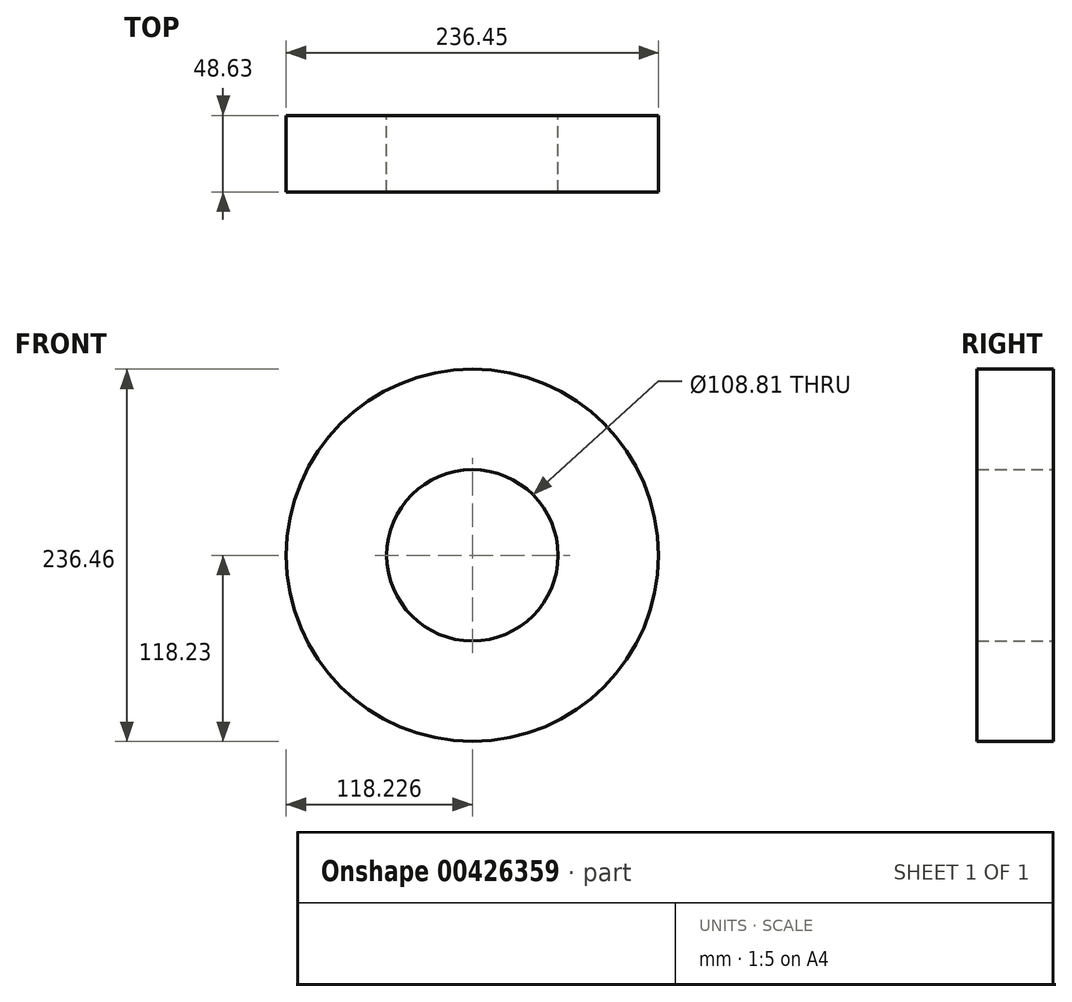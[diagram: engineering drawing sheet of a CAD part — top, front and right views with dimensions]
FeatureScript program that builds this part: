
annotation { "Feature Type Name" : "Feature", "Feature Type Description" : "" }
export const myFeature = defineFeature(function(context is Context, id is Id, definition is map)
    precondition{}
    {
        {
            var Q0;
            Q0=qCreatedBy(makeId("Top.planeOp"),FACE);
            var sketch = newSketch(context, id + "F0", { "sketchPlane" : qUnion([Q0])});
            skLineSegment(sketch, "E0.bottom", {"start": v(0, 0) * mm, "end": v(63.82, 0) * mm});
            skLineSegment(sketch, "E0.top", {"start": v(0, 48.63) * mm, "end": v(63.82, 48.63) * mm});
            skLineSegment(sketch, "E0.left", {"start": v(0, 0) * mm, "end": v(0, 48.63) * mm});
            skLineSegment(sketch, "E0.right", {"start": v(63.82, 0) * mm, "end": v(63.82, 48.63) * mm});
            skSolve(sketch);
        }
        {
            var Q0;
            Q0=qCreatedBy(makeId("Top.planeOp"),FACE);
            var sketch = newSketch(context, id + "F1", { "sketchPlane" : qUnion([Q0])});
            skLineSegment(sketch, "E1", {"start": v(-54.4, 19.8) * mm, "end": v(-54.4, -32.55) * mm});
            skSolve(sketch);
        }
        {
            var Q0;
            Q0=makeQuery(id+"F0.imprint","IMPRINT",FACE,{"disambiguationData":[TD([[makeQuery(id+"F0.imprint","IMPRINT",EDGE,{"derivedFrom":sQuery(id+"F0.wireOp",EDGE,"E0.bottom")}),1.0]])]});
            var Q1;
            Q1=sQuery(id+"F1.wireOp",EDGE,"E1");
            revolve(context, id + "F2", {"entities" : qUnion([Q0]), "axis" : qUnion([Q1]), "revolveType" : RevolveType.FULL});
        }
    });
